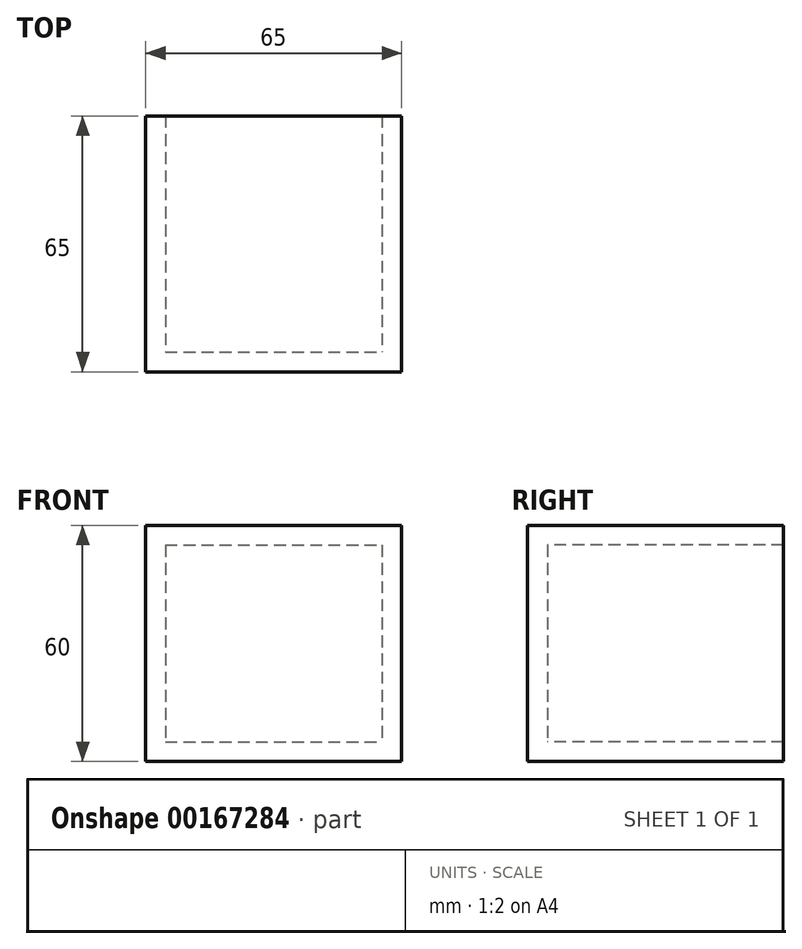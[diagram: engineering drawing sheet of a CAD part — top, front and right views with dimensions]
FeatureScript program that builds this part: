
annotation { "Feature Type Name" : "Feature", "Feature Type Description" : "" }
export const myFeature = defineFeature(function(context is Context, id is Id, definition is map)
    precondition{}
    {
        {
            var Q0;
            Q0=qCreatedBy(makeId("Top.planeOp"),FACE);
            var sketch = newSketch(context, id + "F0", { "sketchPlane" : qUnion([Q0])});
            skLineSegment(sketch, "E0.bottom", {"start": v(-30, 32.5) * mm, "end": v(35, 32.5) * mm});
            skLineSegment(sketch, "E0.top", {"start": v(-30, -32.5) * mm, "end": v(35, -32.5) * mm});
            skLineSegment(sketch, "E0.left", {"start": v(-30, 32.5) * mm, "end": v(-30, -32.5) * mm});
            skLineSegment(sketch, "E0.right", {"start": v(35, 32.5) * mm, "end": v(35, -32.5) * mm});
            skPoint(sketch, "E0.middle", {"position": v(0, 0) * mm});
            skSolve(sketch);
        }
        {
            var Q0;
            Q0=makeQuery(id+"F0.imprint","IMPRINT",FACE,{"disambiguationData":[TD([[makeQuery(id+"F0.imprint","IMPRINT",EDGE,{"derivedFrom":sQuery(id+"F0.wireOp",EDGE,"E0.bottom")}),-1.0]])]});
            extrude(context, id + "F1", {"entities" : qUnion([Q0]), "endBound" : BoundingType.SYMMETRIC, "depth" : 60 * mm});
        }
        {
            var Q0;
            Q0=makeQuery(id+"F1.opExtrude","SWEPT_FACE",FACE,{"disambiguationData":[OSD([sQuery(id+"F0.wireOp",EDGE,"E0.bottom")])]});
            shell(context, id + "F2", {"entities" : qUnion([Q0]), "thickness" : 5 * mm});
        }
    });
